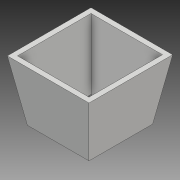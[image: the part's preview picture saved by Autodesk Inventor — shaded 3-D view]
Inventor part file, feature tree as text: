
AUTODESK INVENTOR PART (.ipt)
format: ipt  version: 2017 (Build 210142000, 142)  size: 97,792 bytes
history: native  units: mm
features: sketch x2, plane x1, loft x1, shell x1
ambient origin geometry x8: Origin, YZ Plane, XZ Plane, XY Plane, X Axis, Y Axis, Z Axis, Center Point
bodies: Solid1 (feature_tree)
feature tree (5):
  sketch  "Sketch1"  dims[d0=49.5mm d1=51.5mm d2=6.0mm]
  plane  "Work Plane1"
  loft  "Loft1"
  shell  "Shell1"  Thickness=6.0mm
  sketch  "Sketch2"  dims[d3=6.0mm d4=6.0mm d5=6.0mm d6=60.0mm d7=10.0mm d8=10.0mm d9=10.0mm d10=10.0mm d11=0.0mm d12=90.0deg d13=0.0mm d14=90.0deg d15=5.0mm]
